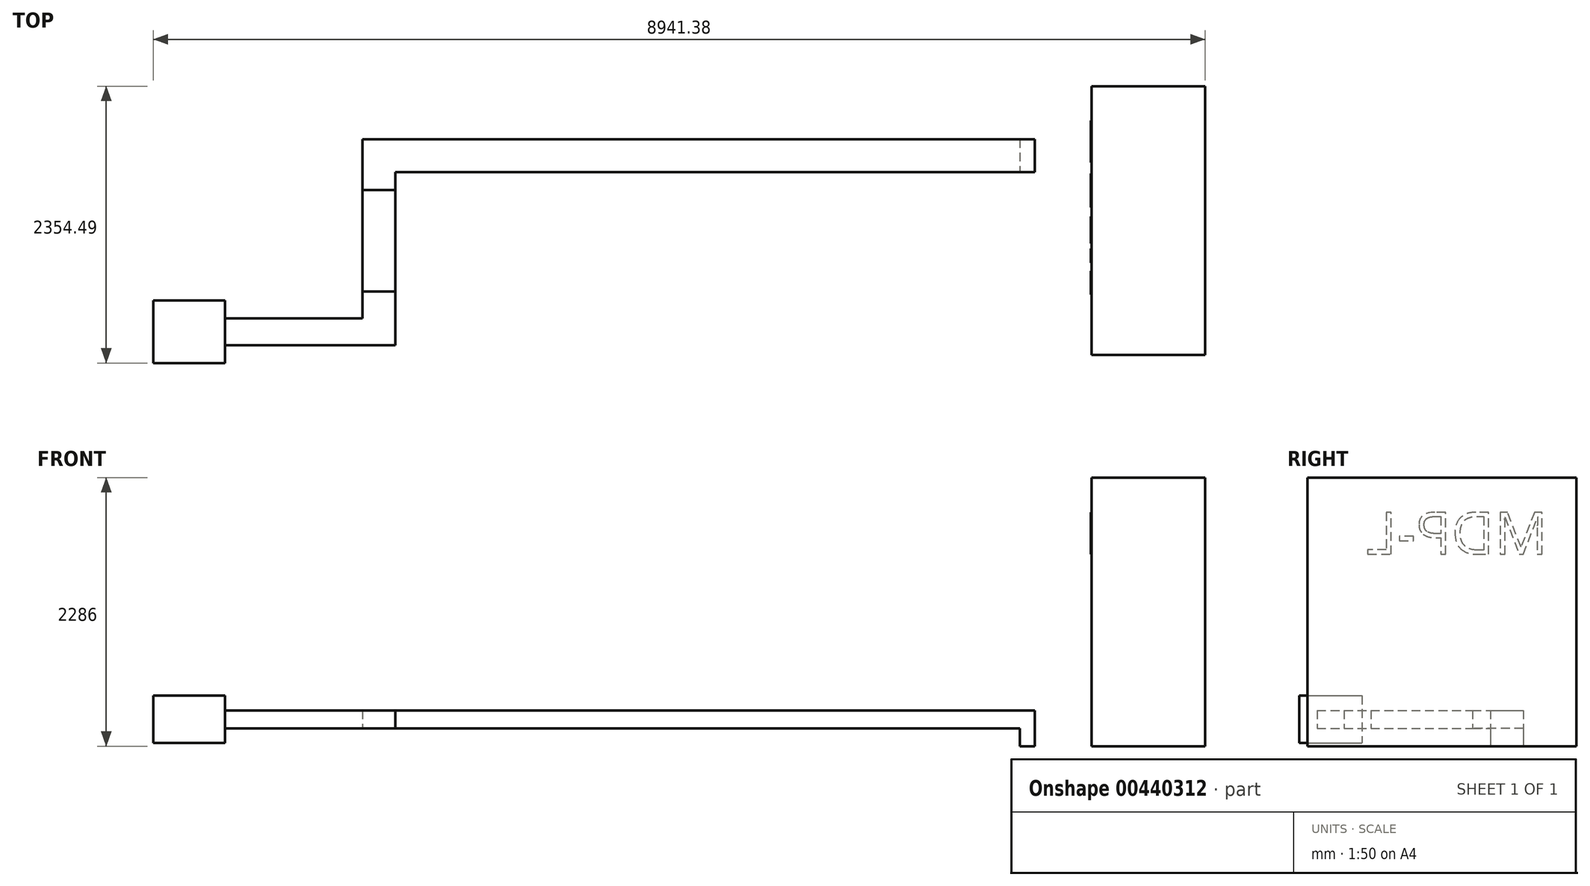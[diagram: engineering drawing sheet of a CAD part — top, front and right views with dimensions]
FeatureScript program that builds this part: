
annotation { "Feature Type Name" : "Feature", "Feature Type Description" : "" }
export const myFeature = defineFeature(function(context is Context, id is Id, definition is map)
    precondition{}
    {
        {
            var Q0;
            Q0=qCreatedBy(makeId("Top.planeOp"),FACE);
            var sketch = newSketch(context, id + "F0", { "sketchPlane" : qUnion([Q0])});
            skLineSegment(sketch, "E0.bottom", {"start": v(0, 0) * mm, "end": v(965.2, 0) * mm});
            skLineSegment(sketch, "E0.top", {"start": v(0, -2286) * mm, "end": v(965.2, -2286) * mm});
            skLineSegment(sketch, "E0.left", {"start": v(0, 0) * mm, "end": v(0, -2286) * mm});
            skLineSegment(sketch, "E0.right", {"start": v(965.2, 0) * mm, "end": v(965.2, -2286) * mm});
            skSolve(sketch);
        }
        {
            var Q0;
            Q0=makeQuery(id+"F0.imprint","IMPRINT",FACE,{"disambiguationData":[TD([[makeQuery(id+"F0.imprint","IMPRINT",EDGE,{"derivedFrom":sQuery(id+"F0.wireOp",EDGE,"E0.bottom")}),-1.0]])]});
            extrude(context, id + "F1", {"entities" : qUnion([Q0]), "depth" : 2286 * mm});
        }
        {
            var Q0;
            Q0=qCreatedBy(makeId("Top.planeOp"),FACE);
            var sketch = newSketch(context, id + "F2", { "sketchPlane" : qUnion([Q0])});
            skLineSegment(sketch, "E1.bottom", {"start": v(-610.18, -729.26) * mm, "end": v(-483.18, -729.26) * mm});
            skLineSegment(sketch, "E1.top", {"start": v(-610.18, -449.86) * mm, "end": v(-483.18, -449.86) * mm});
            skLineSegment(sketch, "E1.left", {"start": v(-610.18, -729.26) * mm, "end": v(-610.18, -449.86) * mm});
            skLineSegment(sketch, "E1.right", {"start": v(-483.18, -729.26) * mm, "end": v(-483.18, -449.86) * mm});
            skSolve(sketch);
        }
        {
            var Q0;
            Q0=makeQuery(id+"F2.imprint","IMPRINT",FACE,{"disambiguationData":[TD([[makeQuery(id+"F2.imprint","IMPRINT",EDGE,{"derivedFrom":sQuery(id+"F2.wireOp",EDGE,"E1.bottom")}),1.0]])]});
            extrude(context, id + "F3", {"entities" : qUnion([Q0]), "depth" : 304.8 * mm});
        }
        {
            var Q0;
            Q0=makeQuery(id+"F3.opExtrude","SWEPT_FACE",FACE,{"disambiguationData":[OSD([sQuery(id+"F2.wireOp",EDGE,"E1.left")])]});
            var sketch = newSketch(context, id + "F4", { "sketchPlane" : qUnion([Q0])});
            skLineSegment(sketch, "E2.bottom", {"start": v(449.86, 304.8) * mm, "end": v(729.26, 304.8) * mm});
            skLineSegment(sketch, "E2.top", {"start": v(449.86, 152.4) * mm, "end": v(729.26, 152.4) * mm});
            skLineSegment(sketch, "E2.left", {"start": v(449.86, 304.8) * mm, "end": v(449.86, 152.4) * mm});
            skLineSegment(sketch, "E2.right", {"start": v(729.26, 304.8) * mm, "end": v(729.26, 152.4) * mm});
            skSolve(sketch);
        }
        {
            var Q0;
            Q0=makeQuery(id+"F4.imprint","IMPRINT",FACE,{"disambiguationData":[TD([[makeQuery(id+"F4.imprint","IMPRINT",EDGE,{"derivedFrom":sQuery(id+"F4.wireOp",EDGE,"E2.bottom")}),1.0]])]});
            extrude(context, id + "F5", {"entities" : qUnion([Q0]), "operationType" : NewBodyOperationType.ADD, "depth" : 2286 * mm});
        }
        {
            var Q0;
            Q0=makeQuery(id+"F5.opExtrude","CAP_FACE",FACE,{"disambiguationData":[OSD([sQuery(id+"F4.wireOp",EDGE,"E2.bottom"),sQuery(id+"F4.wireOp",EDGE,"E2.top"),sQuery(id+"F4.wireOp",EDGE,"E2.left"),sQuery(id+"F4.wireOp",EDGE,"E2.right")])],"isStart":false});
            extrude(context, id + "F6", {"entities" : qUnion([Q0]), "operationType" : NewBodyOperationType.ADD, "depth" : 2286 * mm});
        }
        {
            var Q0;
            Q0=makeQuery(id+"F6.opExtrude","CAP_FACE",FACE,{"disambiguationData":[OSD([sQuery(id+"F4.wireOp",EDGE,"E2.bottom"),sQuery(id+"F4.wireOp",EDGE,"E2.top"),sQuery(id+"F4.wireOp",EDGE,"E2.left"),sQuery(id+"F4.wireOp",EDGE,"E2.right")])],"isStart":false});
            extrude(context, id + "F7", {"entities" : qUnion([Q0]), "operationType" : NewBodyOperationType.ADD, "depth" : 1016 * mm});
        }
        {
            var Q0;
            {var subQ0=sQuery(id+"F4.wireOp",EDGE,"E2.right");Q0=makeQuery(id+"F7.boolean.opBoolean","MERGE",FACE,{"derivedFrom":[makeQuery(id+"F6.boolean.opBoolean","MERGE",FACE,{"derivedFrom":[makeQuery(id+"F5.boolean.opBoolean","MERGE",FACE,{"derivedFrom":[makeQuery(id+"F3.opExtrude","SWEPT_FACE",FACE,{"disambiguationData":[OSD([sQuery(id+"F2.wireOp",EDGE,"E1.bottom")])]}),makeQuery(id+"F5.opExtrude","SWEPT_FACE",FACE,{"disambiguationData":[OSD([subQ0])]})]}),makeQuery(id+"F6.opExtrude","SWEPT_FACE",FACE,{"disambiguationData":[OSD([subQ0])]})]}),makeQuery(id+"F7.opExtrude","SWEPT_FACE",FACE,{"disambiguationData":[OSD([subQ0])]})]});}
            var sketch = newSketch(context, id + "F8", { "sketchPlane" : qUnion([Q0])});
            skLineSegment(sketch, "E3.bottom", {"start": v(-6198.18, 304.8) * mm, "end": v(-5918.78, 304.8) * mm});
            skLineSegment(sketch, "E3.top", {"start": v(-6198.18, 152.4) * mm, "end": v(-5918.78, 152.4) * mm});
            skLineSegment(sketch, "E3.left", {"start": v(-6198.18, 304.8) * mm, "end": v(-6198.18, 152.4) * mm});
            skLineSegment(sketch, "E3.right", {"start": v(-5918.78, 304.8) * mm, "end": v(-5918.78, 152.4) * mm});
            skSolve(sketch);
        }
        {
            var Q0;
            Q0=makeQuery(id+"F8.imprint","IMPRINT",FACE,{"disambiguationData":[TD([[makeQuery(id+"F8.imprint","IMPRINT",EDGE,{"derivedFrom":sQuery(id+"F8.wireOp",EDGE,"E3.bottom")}),-1.0]])]});
            extrude(context, id + "F9", {"entities" : qUnion([Q0]), "operationType" : NewBodyOperationType.ADD, "depth" : 152.4 * mm});
        }
        {
            var Q0;
            Q0=makeQuery(id+"F9.opExtrude","CAP_FACE",FACE,{"disambiguationData":[OSD([sQuery(id+"F8.wireOp",EDGE,"E3.bottom"),sQuery(id+"F8.wireOp",EDGE,"E3.top"),sQuery(id+"F8.wireOp",EDGE,"E3.left"),sQuery(id+"F8.wireOp",EDGE,"E3.right")])],"isStart":false});
            extrude(context, id + "F10", {"entities" : qUnion([Q0]), "depth" : 863.6 * mm});
        }
        {
            var Q0;
            Q0=makeQuery(id+"F10.opExtrude","CAP_FACE",FACE,{"disambiguationData":[OSD([sQuery(id+"F8.wireOp",EDGE,"E3.bottom"),sQuery(id+"F8.wireOp",EDGE,"E3.top"),sQuery(id+"F8.wireOp",EDGE,"E3.left"),sQuery(id+"F8.wireOp",EDGE,"E3.right")])],"isStart":false});
            extrude(context, id + "F11", {"entities" : qUnion([Q0]), "depth" : 457.2 * mm});
        }
        {
            var Q0;
            Q0=makeQuery(id+"F11.opExtrude","SWEPT_FACE",FACE,{"disambiguationData":[OSD([sQuery(id+"F8.wireOp",EDGE,"E3.left")])]});
            var sketch = newSketch(context, id + "F12", { "sketchPlane" : qUnion([Q0])});
            skLineSegment(sketch, "E4.bottom", {"start": v(2202.46, 304.8) * mm, "end": v(1973.86, 304.8) * mm});
            skLineSegment(sketch, "E4.top", {"start": v(2202.46, 152.4) * mm, "end": v(1973.86, 152.4) * mm});
            skLineSegment(sketch, "E4.left", {"start": v(2202.46, 304.8) * mm, "end": v(2202.46, 152.4) * mm});
            skLineSegment(sketch, "E4.right", {"start": v(1973.86, 304.8) * mm, "end": v(1973.86, 152.4) * mm});
            skSolve(sketch);
        }
        {
            var Q0;
            Q0=makeQuery(id+"F12.imprint","IMPRINT",FACE,{"disambiguationData":[TD([[makeQuery(id+"F12.imprint","IMPRINT",EDGE,{"derivedFrom":sQuery(id+"F12.wireOp",EDGE,"E4.bottom")}),1.0]])]});
            extrude(context, id + "F13", {"entities" : qUnion([Q0]), "operationType" : NewBodyOperationType.ADD, "depth" : 1778 * mm});
        }
        {
            var Q0;
            Q0=makeQuery(id+"F13.opExtrude","CAP_FACE",FACE,{"disambiguationData":[OSD([sQuery(id+"F12.wireOp",EDGE,"E4.bottom"),sQuery(id+"F12.wireOp",EDGE,"E4.top"),sQuery(id+"F12.wireOp",EDGE,"E4.left"),sQuery(id+"F12.wireOp",EDGE,"E4.right")])],"isStart":false});
            var sketch = newSketch(context, id + "F14", { "sketchPlane" : qUnion([Q0])});
            skLineSegment(sketch, "E5.bottom", {"start": v(2354.49, 430.58) * mm, "end": v(1821.83, 430.58) * mm});
            skLineSegment(sketch, "E5.top", {"start": v(2354.49, 26.62) * mm, "end": v(1821.83, 26.62) * mm});
            skLineSegment(sketch, "E5.left", {"start": v(2354.49, 430.58) * mm, "end": v(2354.49, 26.62) * mm});
            skLineSegment(sketch, "E5.right", {"start": v(1821.83, 430.58) * mm, "end": v(1821.83, 26.62) * mm});
            skPoint(sketch, "E5.middle", {"position": v(2088.16, 228.6) * mm});
            skPoint(sketch, "E5.middle.positionSnap0", {"position": v(2202.46, 228.6) * mm});
            skPoint(sketch, "E5.middle.positionSnap1", {"position": v(2088.16, 152.4) * mm});
            skPoint(sketch, "E5.centerSnap0", {"position": v(2202.46, 228.6) * mm});
            skPoint(sketch, "E5.centerSnap1", {"position": v(2088.16, 152.4) * mm});
            skSolve(sketch);
        }
        {
            var Q0;
            Q0=makeQuery(id+"F14.imprint","IMPRINT",FACE,{"disambiguationData":[TD([[makeQuery(id+"F14.imprint","IMPRINT",EDGE,{"derivedFrom":sQuery(id+"F14.wireOp",EDGE,"E5.bottom")}),1.0]])]});
            extrude(context, id + "F15", {"entities" : qUnion([Q0]), "operationType" : NewBodyOperationType.ADD, "oppositeDirection" : true, "depth" : 609.6 * mm});
        }
        {
            var Q0;
            Q0=makeQuery(id+"F1.opExtrude","SWEPT_FACE",FACE,{"disambiguationData":[OSD([sQuery(id+"F0.wireOp",EDGE,"E0.left")])]});
            var sketch = newSketch(context, id + "F16", { "sketchPlane" : qUnion([Q0])});
            skText(sketch, "E6", { "text": "MDP-L", "fontName": "OpenSans-Regular.ttf"});
            const initialGuessF16  = {"E6": [0.24299, 1.6328, 1, 0, 0.36075]};
            skSetInitialGuess(sketch, initialGuessF16);
            skSolve(sketch);
        }
        {
            var Q0;
            Q0 = qSketchRegion(id + "F16", true);
            extrude(context, id + "F17", {"entities" : qUnion([Q0]), "operationType" : NewBodyOperationType.ADD, "depth" : 5.08 * mm});
        }
    });
